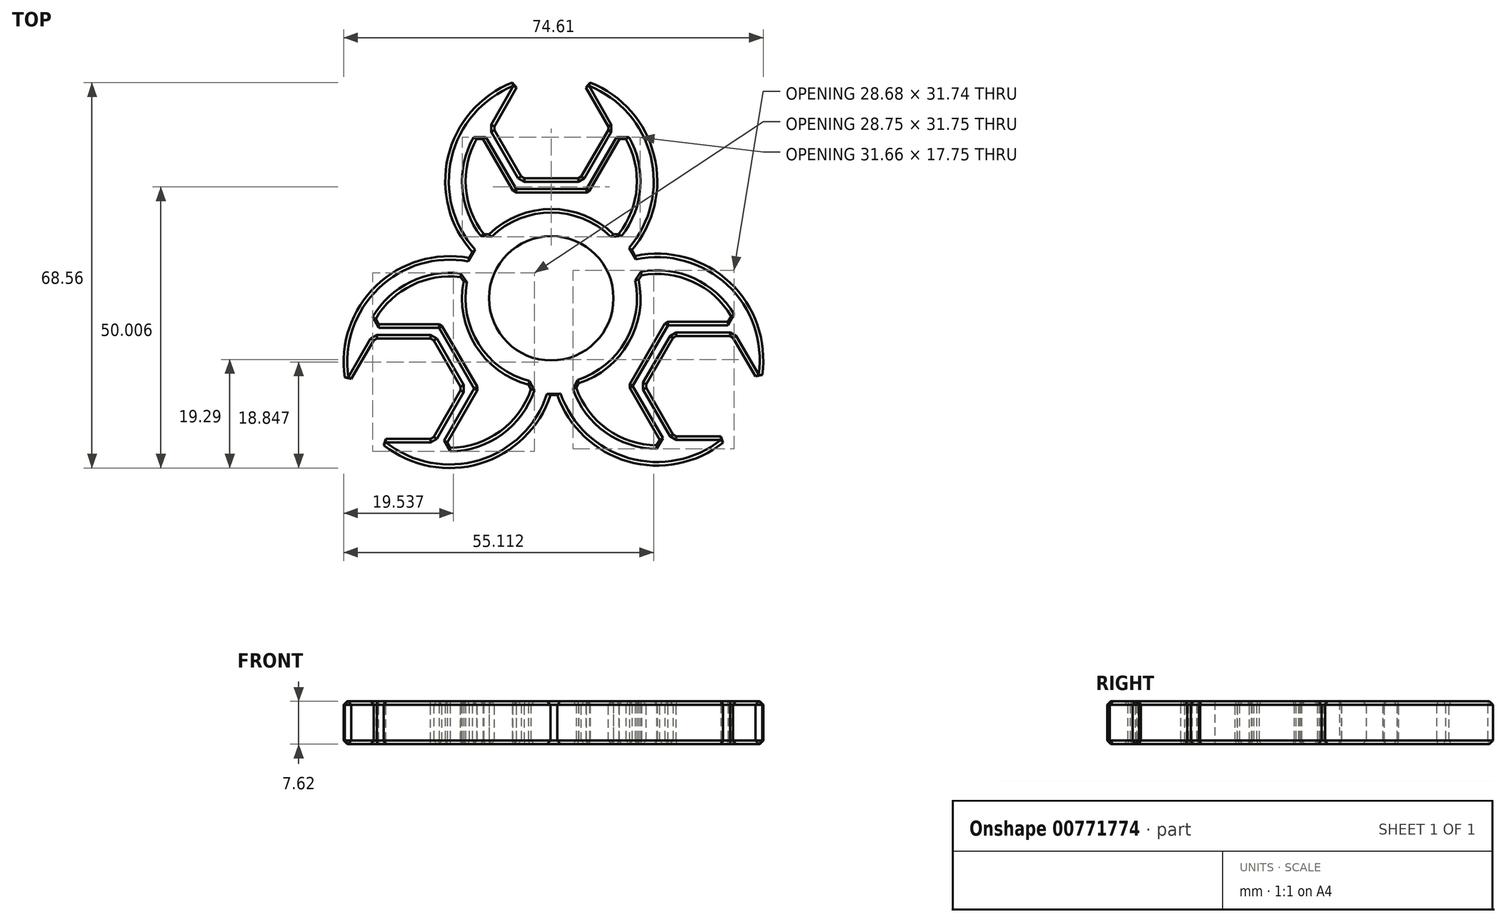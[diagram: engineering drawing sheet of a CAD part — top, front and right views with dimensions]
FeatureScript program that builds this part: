
annotation { "Feature Type Name" : "Feature", "Feature Type Description" : "" }
export const myFeature = defineFeature(function(context is Context, id is Id, definition is map)
    precondition{}
    {
        {
            var Q0;
            Q0=qCreatedBy(makeId("Top.planeOp"),FACE);
            var sketch = newSketch(context, id + "F0", { "sketchPlane" : qUnion([Q0])});
            skCircle(sketch, "E0", {"center": v(0, 0) * mm, "radius": 11.06 * mm});
            skCircle(sketch, "E1", {"center": v(0, 0) * mm, "radius": 15.88 * mm});
            skLineSegment(sketch, "E2", {"start": v(0, 0) * mm, "end": v(0, 15.88) * mm, "construction": true});
            skLineSegment(sketch, "E3", {"start": v(13.75, 7.94) * mm, "end": v(-13.75, 7.94) * mm, "construction": true});
            skPoint(sketch, "E3.startSnap0", {"position": v(0, 7.94) * mm});
            skLineSegment(sketch, "E4", {"start": v(0, 7.94) * mm, "end": v(0, 0) * mm, "construction": true});
            skLineSegment(sketch, "E5", {"start": v(0, 3.97) * mm, "end": v(0, 0) * mm, "construction": true});
            skCircle(sketch, "E6", {"center": v(0, 20.84) * mm, "radius": 18.85 * mm});
            skPoint(sketch, "E6.first.point", {"position": v(0, 1.98) * mm});
            skCircle(sketch, "E7", {"center": v(0, 20.84) * mm, "radius": 15.24 * mm});
            skLineSegment(sketch, "E8", {"start": v(0, 20.84) * mm, "end": v(0, 39.69) * mm, "construction": true});
            skPoint(sketch, "E9.0.midPoint", {"position": v(0, 45.97) * mm});
            skLineSegment(sketch, "E10", {"start": v(0, 20.84) * mm, "end": v(0, 30.26) * mm, "construction": true});
            skCircle(sketch, "E11.cCircle", {"center": v(0, 30.26) * mm, "radius": 8.93 * mm, "construction": true});
            skLineSegment(sketch, "E11.0", {"start": v(-5.16, 39.2) * mm, "end": v(5.16, 39.2) * mm});
            skLineSegment(sketch, "E11.1", {"start": v(5.16, 39.2) * mm, "end": v(10.31, 30.26) * mm});
            skLineSegment(sketch, "E11.2", {"start": v(10.31, 30.26) * mm, "end": v(5.16, 21.33) * mm});
            skLineSegment(sketch, "E11.3", {"start": v(5.16, 21.33) * mm, "end": v(-5.16, 21.33) * mm});
            skLineSegment(sketch, "E11.4", {"start": v(-5.16, 21.33) * mm, "end": v(-10.31, 30.26) * mm});
            skLineSegment(sketch, "E11.5", {"start": v(-10.31, 30.26) * mm, "end": v(-5.16, 39.2) * mm});
            skPoint(sketch, "E11.0.midPoint", {"position": v(0, 39.2) * mm});
            skLineSegment(sketch, "E12.1.0", {"start": v(-31.39, -7.13) * mm, "end": v(-21.08, -7.13) * mm});
            skPoint(sketch, "E12.1.1", {"position": v(-1.74, -1.93) * mm});
            skPoint(sketch, "E12.1.2", {"position": v(-6.9, -4.9) * mm});
            skLineSegment(sketch, "E12.1.3", {"start": v(-15.92, -16.06) * mm, "end": v(-21.08, -25) * mm});
            skPoint(sketch, "E12.1.4", {"position": v(-33.97, -20.53) * mm});
            skLineSegment(sketch, "E12.1.5", {"start": v(-21.08, -7.13) * mm, "end": v(-15.92, -16.06) * mm});
            skLineSegment(sketch, "E12.1.6", {"start": v(-18.07, -11.35) * mm, "end": v(-34.4, -20.78) * mm, "construction": true});
            skCircle(sketch, "E12.1.7", {"center": v(-18.07, -11.35) * mm, "radius": 18.85 * mm});
            skLineSegment(sketch, "E12.1.8", {"start": v(-18.07, -11.35) * mm, "end": v(-26.23, -16.06) * mm, "construction": true});
            skLineSegment(sketch, "E12.1.9", {"start": v(-31.39, -25) * mm, "end": v(-36.54, -16.06) * mm});
            skCircle(sketch, "E12.1.10", {"center": v(-26.23, -16.06) * mm, "radius": 8.93 * mm, "construction": true});
            skLineSegment(sketch, "E12.1.11", {"start": v(-36.54, -16.06) * mm, "end": v(-31.39, -7.13) * mm});
            skLineSegment(sketch, "E12.1.12", {"start": v(-13.77, 7) * mm, "end": v(-0.02, -16.8) * mm, "construction": true});
            skLineSegment(sketch, "E12.1.13", {"start": v(-21.08, -25) * mm, "end": v(-31.39, -25) * mm});
            skCircle(sketch, "E12.1.14", {"center": v(-18.07, -11.35) * mm, "radius": 15.24 * mm});
            skLineSegment(sketch, "E12.2.0", {"start": v(21.85, -24.55) * mm, "end": v(16.7, -15.62) * mm});
            skPoint(sketch, "E12.2.1", {"position": v(2.52, -1.48) * mm});
            skPoint(sketch, "E12.2.2", {"position": v(7.67, -4.46) * mm});
            skLineSegment(sketch, "E12.2.3", {"start": v(21.85, -6.69) * mm, "end": v(32.16, -6.69) * mm});
            skPoint(sketch, "E12.2.4", {"position": v(34.74, -20.08) * mm});
            skLineSegment(sketch, "E12.2.5", {"start": v(16.7, -15.62) * mm, "end": v(21.85, -6.69) * mm});
            skLineSegment(sketch, "E12.2.6", {"start": v(18.84, -10.9) * mm, "end": v(35.17, -20.33) * mm, "construction": true});
            skCircle(sketch, "E12.2.7", {"center": v(18.84, -10.9) * mm, "radius": 18.85 * mm});
            skLineSegment(sketch, "E12.2.8", {"start": v(18.84, -10.9) * mm, "end": v(27, -15.62) * mm, "construction": true});
            skLineSegment(sketch, "E12.2.9", {"start": v(37.32, -15.62) * mm, "end": v(32.16, -24.55) * mm});
            skCircle(sketch, "E12.2.10", {"center": v(27, -15.62) * mm, "radius": 8.93 * mm, "construction": true});
            skLineSegment(sketch, "E12.2.11", {"start": v(32.16, -24.55) * mm, "end": v(21.85, -24.55) * mm});
            skLineSegment(sketch, "E12.2.12", {"start": v(0.8, -16.36) * mm, "end": v(14.54, 7.45) * mm, "construction": true});
            skLineSegment(sketch, "E12.2.13", {"start": v(32.16, -6.69) * mm, "end": v(37.32, -15.62) * mm});
            skCircle(sketch, "E12.2.14", {"center": v(18.84, -10.9) * mm, "radius": 15.24 * mm});
            skPoint(sketch, "E12.center", {"position": v(0.26, -0.47) * mm});
            skCircle(sketch, "E13.cCircle", {"center": v(0, 30.26) * mm, "radius": 11.47 * mm, "construction": true});
            skLineSegment(sketch, "E13.0", {"start": v(-6.62, 41.73) * mm, "end": v(6.62, 41.73) * mm});
            skLineSegment(sketch, "E13.1", {"start": v(6.62, 41.73) * mm, "end": v(13.25, 30.26) * mm});
            skLineSegment(sketch, "E13.2", {"start": v(13.25, 30.26) * mm, "end": v(6.62, 18.8) * mm});
            skLineSegment(sketch, "E13.3", {"start": v(6.62, 18.8) * mm, "end": v(-6.62, 18.8) * mm});
            skLineSegment(sketch, "E13.4", {"start": v(-6.62, 18.8) * mm, "end": v(-13.25, 30.26) * mm});
            skLineSegment(sketch, "E13.5", {"start": v(-13.25, 30.26) * mm, "end": v(-6.62, 41.73) * mm});
            skPoint(sketch, "E13.0.midPoint", {"position": v(0, 41.73) * mm});
            skCircle(sketch, "E14.cCircle", {"center": v(27, -15.62) * mm, "radius": 11.47 * mm, "construction": true});
            skLineSegment(sketch, "E14.0", {"start": v(40.25, -15.62) * mm, "end": v(33.63, -27.09) * mm});
            skLineSegment(sketch, "E14.1", {"start": v(33.63, -27.09) * mm, "end": v(20.38, -27.09) * mm});
            skLineSegment(sketch, "E14.2", {"start": v(20.38, -27.09) * mm, "end": v(13.76, -15.62) * mm});
            skLineSegment(sketch, "E14.3", {"start": v(13.76, -15.62) * mm, "end": v(20.38, -4.15) * mm});
            skLineSegment(sketch, "E14.4", {"start": v(20.38, -4.15) * mm, "end": v(33.63, -4.15) * mm});
            skLineSegment(sketch, "E14.5", {"start": v(33.63, -4.15) * mm, "end": v(40.25, -15.62) * mm});
            skPoint(sketch, "E14.0.midPoint", {"position": v(36.94, -21.35) * mm});
            skCircle(sketch, "E15.cCircle", {"center": v(-26.23, -16.06) * mm, "radius": 11.47 * mm, "construction": true});
            skLineSegment(sketch, "E15.0", {"start": v(-32.85, -27.54) * mm, "end": v(-39.48, -16.06) * mm});
            skLineSegment(sketch, "E15.1", {"start": v(-39.48, -16.06) * mm, "end": v(-32.85, -4.6) * mm});
            skLineSegment(sketch, "E15.2", {"start": v(-32.85, -4.6) * mm, "end": v(-19.6, -4.6) * mm});
            skLineSegment(sketch, "E15.3", {"start": v(-19.6, -4.6) * mm, "end": v(-12.99, -16.06) * mm});
            skLineSegment(sketch, "E15.4", {"start": v(-12.99, -16.06) * mm, "end": v(-19.6, -27.54) * mm});
            skLineSegment(sketch, "E15.5", {"start": v(-19.6, -27.54) * mm, "end": v(-32.85, -27.54) * mm});
            skPoint(sketch, "E15.0.midPoint", {"position": v(-36.17, -21.8) * mm});
            skSolve(sketch);
        }
        {
            var Q0;
            {var subQ1=sQuery(id+"F0.wireOp",EDGE,"E6");var subQ7=sQuery(id+"F0.wireOp",EDGE,"E13.5");var subQ9=makeQuery(id+"F0.imprint","INTERSECT",VERTEX,{"derivedFrom":[subQ1,subQ7]});Q0=makeQuery(id+"F0.imprint","IMPRINT",FACE,{"disambiguationData":[TD([[makeQuery(id+"F0.imprint","IMPRINT",EDGE,{"disambiguationData":[TD([[subQ9,1.0]])],"derivedFrom":subQ1}),1.0]])]});}
            var Q1;
            {var subQ1=sQuery(id+"F0.wireOp",EDGE,"E1");var subQ5=sQuery(id+"F0.wireOp",EDGE,"E6");var subQ6=makeQuery(id+"F0.imprint","INTERSECT",VERTEX,{"disambiguationData":[OD(1.0)],"derivedFrom":[subQ1,subQ5]});Q1=makeQuery(id+"F0.imprint","IMPRINT",FACE,{"disambiguationData":[TD([[makeQuery(id+"F0.imprint","IMPRINT",EDGE,{"disambiguationData":[TD([[subQ6,1.0]])],"derivedFrom":subQ1}),-1.0]])]});}
            var Q2;
            {var subQ0=sQuery(id+"F0.wireOp",EDGE,"E11.2");Q2=makeQuery(id+"F0.imprint","IMPRINT",FACE,{"disambiguationData":[TD([[makeQuery(id+"F0.imprint","IMPRINT",EDGE,{"derivedFrom":subQ0}),1.0]])]});}
            var Q3;
            {var subQ1=sQuery(id+"F0.wireOp",EDGE,"E13.1");var subQ3=sQuery(id+"F0.wireOp",EDGE,"E6");var subQ4=makeQuery(id+"F0.imprint","INTERSECT",VERTEX,{"derivedFrom":[subQ3,subQ1]});Q3=makeQuery(id+"F0.imprint","IMPRINT",FACE,{"disambiguationData":[TD([[makeQuery(id+"F0.imprint","IMPRINT",EDGE,{"disambiguationData":[TD([[subQ4,-1.0]])],"derivedFrom":subQ3}),1.0]])]});}
            var Q4;
            {var subQ3=sQuery(id+"F0.wireOp",EDGE,"E6");var subQ6=sQuery(id+"F0.wireOp",EDGE,"E1");var subQ9=makeQuery(id+"F0.imprint","INTERSECT",VERTEX,{"disambiguationData":[OD(0.0)],"derivedFrom":[subQ6,subQ3]});Q4=makeQuery(id+"F0.imprint","IMPRINT",FACE,{"disambiguationData":[TD([[makeQuery(id+"F0.imprint","IMPRINT",EDGE,{"disambiguationData":[TD([[subQ9,-1.0]])],"derivedFrom":subQ6}),-1.0]])]});}
            var Q5;
            {var subQ0=sQuery(id+"F0.wireOp",EDGE,"E7");var subQ1=sQuery(id+"F0.wireOp",EDGE,"E0");var subQ2=makeQuery(id+"F0.imprint","INTERSECT",VERTEX,{"disambiguationData":[OD(0.0)],"derivedFrom":[subQ1,subQ0]});Q5=makeQuery(id+"F0.imprint","IMPRINT",FACE,{"disambiguationData":[TD([[makeQuery(id+"F0.imprint","IMPRINT",EDGE,{"disambiguationData":[TD([[subQ2,-1.0]])],"derivedFrom":subQ1}),-1.0]])]});}
            var Q6;
            {var subQ3=sQuery(id+"F0.wireOp",EDGE,"E12.2.7");var subQ7=sQuery(id+"F0.wireOp",EDGE,"E0");var subQ9=makeQuery(id+"F0.imprint","INTERSECT",VERTEX,{"disambiguationData":[OD(0.0)],"derivedFrom":[subQ7,subQ3]});Q6=makeQuery(id+"F0.imprint","IMPRINT",FACE,{"disambiguationData":[TD([[makeQuery(id+"F0.imprint","IMPRINT",EDGE,{"disambiguationData":[TD([[subQ9,-1.0]])],"derivedFrom":subQ7}),-1.0]])]});}
            var Q7;
            {var subQ3=sQuery(id+"F0.wireOp",EDGE,"E6");var subQ5=sQuery(id+"F0.wireOp",EDGE,"E0");var subQ6=makeQuery(id+"F0.imprint","INTERSECT",VERTEX,{"disambiguationData":[OD(1.0)],"derivedFrom":[subQ5,subQ3]});Q7=makeQuery(id+"F0.imprint","IMPRINT",FACE,{"disambiguationData":[TD([[makeQuery(id+"F0.imprint","IMPRINT",EDGE,{"disambiguationData":[TD([[subQ6,-1.0]])],"derivedFrom":subQ5}),-1.0]])]});}
            var Q8;
            {var subQ0=sQuery(id+"F0.wireOp",EDGE,"E12.1.7");var subQ1=sQuery(id+"F0.wireOp",EDGE,"E0");var subQ2=makeQuery(id+"F0.imprint","INTERSECT",VERTEX,{"disambiguationData":[OD(0.0)],"derivedFrom":[subQ1,subQ0]});Q8=makeQuery(id+"F0.imprint","IMPRINT",FACE,{"disambiguationData":[TD([[makeQuery(id+"F0.imprint","IMPRINT",EDGE,{"disambiguationData":[TD([[subQ2,-1.0]])],"derivedFrom":subQ1}),-1.0]])]});}
            var Q9;
            {var subQ0=sQuery(id+"F0.wireOp",EDGE,"E7");var subQ1=sQuery(id+"F0.wireOp",EDGE,"E0");var subQ2=makeQuery(id+"F0.imprint","INTERSECT",VERTEX,{"disambiguationData":[OD(1.0)],"derivedFrom":[subQ1,subQ0]});Q9=makeQuery(id+"F0.imprint","IMPRINT",FACE,{"disambiguationData":[TD([[makeQuery(id+"F0.imprint","IMPRINT",EDGE,{"disambiguationData":[TD([[subQ2,-1.0]])],"derivedFrom":subQ1}),-1.0]])]});}
            var Q10;
            {var subQ3=sQuery(id+"F0.wireOp",EDGE,"E6");var subQ5=sQuery(id+"F0.wireOp",EDGE,"E0");var subQ6=makeQuery(id+"F0.imprint","INTERSECT",VERTEX,{"disambiguationData":[OD(0.0)],"derivedFrom":[subQ5,subQ3]});Q10=makeQuery(id+"F0.imprint","IMPRINT",FACE,{"disambiguationData":[TD([[makeQuery(id+"F0.imprint","IMPRINT",EDGE,{"disambiguationData":[TD([[subQ6,1.0]])],"derivedFrom":subQ5}),-1.0]])]});}
            var Q11;
            {var subQ0=sQuery(id+"F0.wireOp",EDGE,"E6");var subQ1=sQuery(id+"F0.wireOp",EDGE,"E0");var subQ2=makeQuery(id+"F0.imprint","INTERSECT",VERTEX,{"disambiguationData":[OD(0.0)],"derivedFrom":[subQ1,subQ0]});Q11=makeQuery(id+"F0.imprint","IMPRINT",FACE,{"disambiguationData":[TD([[makeQuery(id+"F0.imprint","IMPRINT",EDGE,{"disambiguationData":[TD([[subQ2,-1.0]])],"derivedFrom":subQ1}),-1.0]])]});}
            var Q12;
            {var subQ5=sQuery(id+"F0.wireOp",EDGE,"E1");var subQ7=sQuery(id+"F0.wireOp",EDGE,"E12.2.7");var subQ8=makeQuery(id+"F0.imprint","INTERSECT",VERTEX,{"disambiguationData":[OD(0.0)],"derivedFrom":[subQ5,subQ7]});Q12=makeQuery(id+"F0.imprint","IMPRINT",FACE,{"disambiguationData":[TD([[makeQuery(id+"F0.imprint","IMPRINT",EDGE,{"disambiguationData":[TD([[subQ8,1.0]])],"derivedFrom":subQ5}),-1.0]])]});}
            var Q13;
            {var subQ0=sQuery(id+"F0.wireOp",EDGE,"E12.2.14");var subQ1=sQuery(id+"F0.wireOp",EDGE,"E0");var subQ2=makeQuery(id+"F0.imprint","INTERSECT",VERTEX,{"disambiguationData":[OD(0.0)],"derivedFrom":[subQ1,subQ0]});Q13=makeQuery(id+"F0.imprint","IMPRINT",FACE,{"disambiguationData":[TD([[makeQuery(id+"F0.imprint","IMPRINT",EDGE,{"disambiguationData":[TD([[subQ2,1.0]])],"derivedFrom":subQ1}),-1.0]])]});}
            var Q14;
            {var subQ0=sQuery(id+"F0.wireOp",EDGE,"E12.1.14");var subQ1=sQuery(id+"F0.wireOp",EDGE,"E0");var subQ2=makeQuery(id+"F0.imprint","INTERSECT",VERTEX,{"disambiguationData":[OD(0.0)],"derivedFrom":[subQ1,subQ0]});Q14=makeQuery(id+"F0.imprint","IMPRINT",FACE,{"disambiguationData":[TD([[makeQuery(id+"F0.imprint","IMPRINT",EDGE,{"disambiguationData":[TD([[subQ2,-1.0]])],"derivedFrom":subQ1}),-1.0]])]});}
            var Q15;
            {var subQ3=sQuery(id+"F0.wireOp",EDGE,"E12.1.7");var subQ5=sQuery(id+"F0.wireOp",EDGE,"E0");var subQ6=makeQuery(id+"F0.imprint","INTERSECT",VERTEX,{"disambiguationData":[OD(1.0)],"derivedFrom":[subQ5,subQ3]});Q15=makeQuery(id+"F0.imprint","IMPRINT",FACE,{"disambiguationData":[TD([[makeQuery(id+"F0.imprint","IMPRINT",EDGE,{"disambiguationData":[TD([[subQ6,-1.0]])],"derivedFrom":subQ5}),-1.0]])]});}
            var Q16;
            {var subQ0=sQuery(id+"F0.wireOp",EDGE,"E12.2.7");var subQ1=sQuery(id+"F0.wireOp",EDGE,"E0");var subQ2=makeQuery(id+"F0.imprint","INTERSECT",VERTEX,{"disambiguationData":[OD(1.0)],"derivedFrom":[subQ1,subQ0]});Q16=makeQuery(id+"F0.imprint","IMPRINT",FACE,{"disambiguationData":[TD([[makeQuery(id+"F0.imprint","IMPRINT",EDGE,{"disambiguationData":[TD([[subQ2,-1.0]])],"derivedFrom":subQ1}),-1.0]])]});}
            var Q17;
            {var subQ5=sQuery(id+"F0.wireOp",EDGE,"E12.1.14");var subQ6=sQuery(id+"F0.wireOp",EDGE,"E0");var subQ7=makeQuery(id+"F0.imprint","INTERSECT",VERTEX,{"disambiguationData":[OD(1.0)],"derivedFrom":[subQ6,subQ5]});Q17=makeQuery(id+"F0.imprint","IMPRINT",FACE,{"disambiguationData":[TD([[makeQuery(id+"F0.imprint","IMPRINT",EDGE,{"disambiguationData":[TD([[subQ7,-1.0]])],"derivedFrom":subQ6}),-1.0]])]});}
            var Q18;
            {var subQ5=sQuery(id+"F0.wireOp",EDGE,"E12.1.7");var subQ6=sQuery(id+"F0.wireOp",EDGE,"E1");var subQ7=makeQuery(id+"F0.imprint","INTERSECT",VERTEX,{"disambiguationData":[OD(1.0)],"derivedFrom":[subQ6,subQ5]});Q18=makeQuery(id+"F0.imprint","IMPRINT",FACE,{"disambiguationData":[TD([[makeQuery(id+"F0.imprint","IMPRINT",EDGE,{"disambiguationData":[TD([[subQ7,1.0]])],"derivedFrom":subQ6}),-1.0]])]});}
            var Q19;
            {var subQ3=sQuery(id+"F0.wireOp",EDGE,"E12.2.7");var subQ6=sQuery(id+"F0.wireOp",EDGE,"E1");var subQ9=makeQuery(id+"F0.imprint","INTERSECT",VERTEX,{"disambiguationData":[OD(1.0)],"derivedFrom":[subQ6,subQ3]});Q19=makeQuery(id+"F0.imprint","IMPRINT",FACE,{"disambiguationData":[TD([[makeQuery(id+"F0.imprint","IMPRINT",EDGE,{"disambiguationData":[TD([[subQ9,-1.0]])],"derivedFrom":subQ6}),-1.0]])]});}
            var Q20;
            {var subQ0=sQuery(id+"F0.wireOp",EDGE,"E14.5");var subQ7=sQuery(id+"F0.wireOp",EDGE,"E12.2.7");var subQ9=makeQuery(id+"F0.imprint","INTERSECT",VERTEX,{"derivedFrom":[subQ7,subQ0]});Q20=makeQuery(id+"F0.imprint","IMPRINT",FACE,{"disambiguationData":[TD([[makeQuery(id+"F0.imprint","IMPRINT",EDGE,{"disambiguationData":[TD([[subQ9,1.0]])],"derivedFrom":subQ7}),1.0]])]});}
            var Q21;
            {var subQ1=sQuery(id+"F0.wireOp",EDGE,"E12.2.0");Q21=makeQuery(id+"F0.imprint","IMPRINT",FACE,{"disambiguationData":[TD([[makeQuery(id+"F0.imprint","IMPRINT",EDGE,{"derivedFrom":subQ1}),1.0]])]});}
            var Q22;
            {var subQ1=sQuery(id+"F0.wireOp",EDGE,"E14.1");var subQ3=sQuery(id+"F0.wireOp",EDGE,"E12.2.7");var subQ4=makeQuery(id+"F0.imprint","INTERSECT",VERTEX,{"derivedFrom":[subQ3,subQ1]});Q22=makeQuery(id+"F0.imprint","IMPRINT",FACE,{"disambiguationData":[TD([[makeQuery(id+"F0.imprint","IMPRINT",EDGE,{"disambiguationData":[TD([[subQ4,-1.0]])],"derivedFrom":subQ3}),1.0]])]});}
            var Q23;
            {var subQ0=sQuery(id+"F0.wireOp",EDGE,"E15.5");var subQ7=sQuery(id+"F0.wireOp",EDGE,"E12.1.7");var subQ9=makeQuery(id+"F0.imprint","INTERSECT",VERTEX,{"derivedFrom":[subQ7,subQ0]});Q23=makeQuery(id+"F0.imprint","IMPRINT",FACE,{"disambiguationData":[TD([[makeQuery(id+"F0.imprint","IMPRINT",EDGE,{"disambiguationData":[TD([[subQ9,1.0]])],"derivedFrom":subQ7}),1.0]])]});}
            var Q24;
            {var subQ1=sQuery(id+"F0.wireOp",EDGE,"E12.1.0");Q24=makeQuery(id+"F0.imprint","IMPRINT",FACE,{"disambiguationData":[TD([[makeQuery(id+"F0.imprint","IMPRINT",EDGE,{"derivedFrom":subQ1}),1.0]])]});}
            var Q25;
            {var subQ1=sQuery(id+"F0.wireOp",EDGE,"E15.1");var subQ3=sQuery(id+"F0.wireOp",EDGE,"E12.1.7");var subQ4=makeQuery(id+"F0.imprint","INTERSECT",VERTEX,{"derivedFrom":[subQ3,subQ1]});Q25=makeQuery(id+"F0.imprint","IMPRINT",FACE,{"disambiguationData":[TD([[makeQuery(id+"F0.imprint","IMPRINT",EDGE,{"disambiguationData":[TD([[subQ4,-1.0]])],"derivedFrom":subQ3}),1.0]])]});}
            var Q26;
            {var subQ3=sQuery(id+"F0.wireOp",EDGE,"E12.1.7");var subQ6=sQuery(id+"F0.wireOp",EDGE,"E1");var subQ9=makeQuery(id+"F0.imprint","INTERSECT",VERTEX,{"disambiguationData":[OD(0.0)],"derivedFrom":[subQ6,subQ3]});Q26=makeQuery(id+"F0.imprint","IMPRINT",FACE,{"disambiguationData":[TD([[makeQuery(id+"F0.imprint","IMPRINT",EDGE,{"disambiguationData":[TD([[subQ9,-1.0]])],"derivedFrom":subQ6}),-1.0]])]});}
            extrude(context, id + "F1", {"entities" : qUnion([Q0, Q1, Q2, Q3, Q4, Q5, Q6, Q7, Q8, Q9, Q10, Q11, Q12, Q13, Q14, Q15, Q16, Q17, Q18, Q19, Q20, Q21, Q22, Q23, Q24, Q25, Q26]), "depth" : 7.62 * mm, "offsetDistance" : 25.4 * mm, "symmetric" : true});
        }
        {
            var Q0;
            {var subQ0=sQuery(id+"F0.wireOp",EDGE,"E6");var subQ1=makeQuery(id+"F0.imprint","INTERSECT",VERTEX,{"disambiguationData":[OD(1.0)],"derivedFrom":[sQuery(id+"F0.wireOp",EDGE,"E1"),subQ0]});var subQ2=makeQuery(id+"F0.imprint","INTERSECT",VERTEX,{"derivedFrom":[subQ0,sQuery(id+"F0.wireOp",EDGE,"E13.5")]});Q0=makeQuery(id+"F1.opExtrude","CAP_EDGE",EDGE,{"disambiguationData":[OSD([subQ0]),TDD([makeQuery(id+"F0.imprint","IMPRINT",EDGE,{"disambiguationData":[TD([[subQ2,1.0]])],"derivedFrom":subQ0}),makeQuery(id+"F0.imprint","IMPRINT",EDGE,{"disambiguationData":[TD([[subQ1,1.0]])],"derivedFrom":subQ0}),makeQuery(id+"F0.imprint","IMPRINT",EDGE,{"disambiguationData":[TD([[subQ1,-1.0]])],"derivedFrom":subQ0})])],"isStart":false});}
            var Q1;
            {var subQ0=sQuery(id+"F0.wireOp",EDGE,"E7");var subQ1=sQuery(id+"F0.wireOp",EDGE,"E1");Q1=makeQuery(id+"F1.opExtrude","CAP_EDGE",EDGE,{"disambiguationData":[OSD([subQ1]),TDD([makeQuery(id+"F0.imprint","IMPRINT",EDGE,{"disambiguationData":[TD([[makeQuery(id+"F0.imprint","INTERSECT",VERTEX,{"disambiguationData":[OD(0.0)],"derivedFrom":[subQ1,subQ0]}),-1.0]])],"derivedFrom":subQ1})])],"isStart":false});}
            var Q2;
            {var subQ0=sQuery(id+"F0.wireOp",EDGE,"E7");Q2=makeQuery(id+"F1.opExtrude","CAP_EDGE",EDGE,{"disambiguationData":[OSD([subQ0]),TDD([makeQuery(id+"F0.imprint","IMPRINT",EDGE,{"disambiguationData":[TD([[makeQuery(id+"F0.imprint","INTERSECT",VERTEX,{"disambiguationData":[OD(1.0)],"derivedFrom":[sQuery(id+"F0.wireOp",EDGE,"E1"),subQ0]}),1.0]])],"derivedFrom":subQ0})])],"isStart":false});}
            var Q3;
            Q3=makeQuery(id+"F1.opExtrude","CAP_EDGE",EDGE,{"disambiguationData":[OSD([sQuery(id+"F0.wireOp",EDGE,"E13.4")])],"isStart":false});
            var Q4;
            Q4=makeQuery(id+"F1.opExtrude","CAP_EDGE",EDGE,{"disambiguationData":[OSD([sQuery(id+"F0.wireOp",EDGE,"E13.3")])],"isStart":false});
            var Q5;
            Q5=makeQuery(id+"F1.opExtrude","CAP_EDGE",EDGE,{"disambiguationData":[OSD([sQuery(id+"F0.wireOp",EDGE,"E11.3")])],"isStart":false});
            var Q6;
            Q6=makeQuery(id+"F1.opExtrude","CAP_EDGE",EDGE,{"disambiguationData":[OSD([sQuery(id+"F0.wireOp",EDGE,"E11.4")])],"isStart":false});
            var Q7;
            Q7=makeQuery(id+"F1.opExtrude","CAP_EDGE",EDGE,{"disambiguationData":[OSD([sQuery(id+"F0.wireOp",EDGE,"E11.5")])],"isStart":false});
            var Q8;
            Q8=makeQuery(id+"F1.opExtrude","CAP_EDGE",EDGE,{"disambiguationData":[OSD([sQuery(id+"F0.wireOp",EDGE,"E11.1")])],"isStart":false});
            var Q9;
            Q9=makeQuery(id+"F1.opExtrude","CAP_EDGE",EDGE,{"disambiguationData":[OSD([sQuery(id+"F0.wireOp",EDGE,"E11.2")])],"isStart":false});
            var Q10;
            {var subQ0=sQuery(id+"F0.wireOp",EDGE,"E6");var subQ1=makeQuery(id+"F0.imprint","INTERSECT",VERTEX,{"disambiguationData":[OD(0.0)],"derivedFrom":[sQuery(id+"F0.wireOp",EDGE,"E1"),subQ0]});var subQ2=makeQuery(id+"F0.imprint","INTERSECT",VERTEX,{"derivedFrom":[subQ0,sQuery(id+"F0.wireOp",EDGE,"E13.1")]});Q10=makeQuery(id+"F1.opExtrude","CAP_EDGE",EDGE,{"disambiguationData":[OSD([subQ0]),TDD([makeQuery(id+"F0.imprint","IMPRINT",EDGE,{"disambiguationData":[TD([[subQ2,-1.0]])],"derivedFrom":subQ0}),makeQuery(id+"F0.imprint","IMPRINT",EDGE,{"disambiguationData":[TD([[subQ1,1.0]])],"derivedFrom":subQ0}),makeQuery(id+"F0.imprint","IMPRINT",EDGE,{"disambiguationData":[TD([[subQ1,-1.0]])],"derivedFrom":subQ0})])],"isStart":false});}
            var Q11;
            Q11=makeQuery(id+"F1.opExtrude","CAP_EDGE",EDGE,{"disambiguationData":[OSD([sQuery(id+"F0.wireOp",EDGE,"E13.2")])],"isStart":false});
            var Q12;
            {var subQ0=sQuery(id+"F0.wireOp",EDGE,"E7");Q12=makeQuery(id+"F1.opExtrude","CAP_EDGE",EDGE,{"disambiguationData":[OSD([subQ0]),TDD([makeQuery(id+"F0.imprint","IMPRINT",EDGE,{"disambiguationData":[TD([[makeQuery(id+"F0.imprint","INTERSECT",VERTEX,{"disambiguationData":[OD(0.0)],"derivedFrom":[sQuery(id+"F0.wireOp",EDGE,"E1"),subQ0]}),-1.0]])],"derivedFrom":subQ0})])],"isStart":false});}
            var Q13;
            {var subQ0=sQuery(id+"F0.wireOp",EDGE,"E12.2.7");var subQ1=makeQuery(id+"F0.imprint","INTERSECT",VERTEX,{"disambiguationData":[OD(0.0)],"derivedFrom":[sQuery(id+"F0.wireOp",EDGE,"E1"),subQ0]});var subQ2=makeQuery(id+"F0.imprint","INTERSECT",VERTEX,{"derivedFrom":[subQ0,sQuery(id+"F0.wireOp",EDGE,"E14.5")]});Q13=makeQuery(id+"F1.opExtrude","CAP_EDGE",EDGE,{"disambiguationData":[OSD([subQ0]),TDD([makeQuery(id+"F0.imprint","IMPRINT",EDGE,{"disambiguationData":[TD([[subQ2,1.0]])],"derivedFrom":subQ0}),makeQuery(id+"F0.imprint","IMPRINT",EDGE,{"disambiguationData":[TD([[subQ1,1.0]])],"derivedFrom":subQ0}),makeQuery(id+"F0.imprint","IMPRINT",EDGE,{"disambiguationData":[TD([[subQ1,-1.0]])],"derivedFrom":subQ0})])],"isStart":false});}
            var Q14;
            {var subQ0=sQuery(id+"F0.wireOp",EDGE,"E12.2.14");Q14=makeQuery(id+"F1.opExtrude","CAP_EDGE",EDGE,{"disambiguationData":[OSD([subQ0]),TDD([makeQuery(id+"F0.imprint","IMPRINT",EDGE,{"disambiguationData":[TD([[makeQuery(id+"F0.imprint","INTERSECT",VERTEX,{"disambiguationData":[OD(0.0)],"derivedFrom":[sQuery(id+"F0.wireOp",EDGE,"E1"),subQ0]}),1.0]])],"derivedFrom":subQ0})])],"isStart":false});}
            var Q15;
            Q15=makeQuery(id+"F1.opExtrude","CAP_EDGE",EDGE,{"disambiguationData":[OSD([sQuery(id+"F0.wireOp",EDGE,"E12.2.3")])],"isStart":false});
            var Q16;
            Q16=makeQuery(id+"F1.opExtrude","CAP_EDGE",EDGE,{"disambiguationData":[OSD([sQuery(id+"F0.wireOp",EDGE,"E12.2.13")])],"isStart":false});
            var Q17;
            Q17=makeQuery(id+"F1.opExtrude","CAP_EDGE",EDGE,{"disambiguationData":[OSD([sQuery(id+"F0.wireOp",EDGE,"E12.2.5")])],"isStart":false});
            var Q18;
            Q18=makeQuery(id+"F1.opExtrude","CAP_EDGE",EDGE,{"disambiguationData":[OSD([sQuery(id+"F0.wireOp",EDGE,"E12.2.0")])],"isStart":false});
            var Q19;
            Q19=makeQuery(id+"F1.opExtrude","CAP_EDGE",EDGE,{"disambiguationData":[OSD([sQuery(id+"F0.wireOp",EDGE,"E12.2.11")])],"isStart":false});
            var Q20;
            {var subQ0=sQuery(id+"F0.wireOp",EDGE,"E12.2.7");var subQ1=makeQuery(id+"F0.imprint","INTERSECT",VERTEX,{"disambiguationData":[OD(1.0)],"derivedFrom":[sQuery(id+"F0.wireOp",EDGE,"E1"),subQ0]});var subQ2=makeQuery(id+"F0.imprint","INTERSECT",VERTEX,{"derivedFrom":[subQ0,sQuery(id+"F0.wireOp",EDGE,"E14.1")]});Q20=makeQuery(id+"F1.opExtrude","CAP_EDGE",EDGE,{"disambiguationData":[OSD([subQ0]),TDD([makeQuery(id+"F0.imprint","IMPRINT",EDGE,{"disambiguationData":[TD([[subQ2,-1.0]])],"derivedFrom":subQ0}),makeQuery(id+"F0.imprint","IMPRINT",EDGE,{"disambiguationData":[TD([[subQ1,1.0]])],"derivedFrom":subQ0}),makeQuery(id+"F0.imprint","IMPRINT",EDGE,{"disambiguationData":[TD([[subQ1,-1.0]])],"derivedFrom":subQ0})])],"isStart":false});}
            var Q21;
            Q21=makeQuery(id+"F1.opExtrude","CAP_EDGE",EDGE,{"disambiguationData":[OSD([sQuery(id+"F0.wireOp",EDGE,"E14.2")])],"isStart":false});
            var Q22;
            Q22=makeQuery(id+"F1.opExtrude","CAP_EDGE",EDGE,{"disambiguationData":[OSD([sQuery(id+"F0.wireOp",EDGE,"E14.3")])],"isStart":false});
            var Q23;
            Q23=makeQuery(id+"F1.opExtrude","CAP_EDGE",EDGE,{"disambiguationData":[OSD([sQuery(id+"F0.wireOp",EDGE,"E14.4")])],"isStart":false});
            var Q24;
            {var subQ0=sQuery(id+"F0.wireOp",EDGE,"E12.2.14");Q24=makeQuery(id+"F1.opExtrude","CAP_EDGE",EDGE,{"disambiguationData":[OSD([subQ0]),TDD([makeQuery(id+"F0.imprint","IMPRINT",EDGE,{"disambiguationData":[TD([[makeQuery(id+"F0.imprint","INTERSECT",VERTEX,{"disambiguationData":[OD(1.0)],"derivedFrom":[sQuery(id+"F0.wireOp",EDGE,"E1"),subQ0]}),-1.0]])],"derivedFrom":subQ0})])],"isStart":false});}
            var Q25;
            {var subQ0=sQuery(id+"F0.wireOp",EDGE,"E12.2.14");var subQ1=sQuery(id+"F0.wireOp",EDGE,"E1");Q25=makeQuery(id+"F1.opExtrude","CAP_EDGE",EDGE,{"disambiguationData":[OSD([subQ1]),TDD([makeQuery(id+"F0.imprint","IMPRINT",EDGE,{"disambiguationData":[TD([[makeQuery(id+"F0.imprint","INTERSECT",VERTEX,{"disambiguationData":[OD(0.0)],"derivedFrom":[subQ1,subQ0]}),1.0]])],"derivedFrom":subQ1})])],"isStart":false});}
            var Q26;
            {var subQ0=sQuery(id+"F0.wireOp",EDGE,"E12.1.7");var subQ1=makeQuery(id+"F0.imprint","INTERSECT",VERTEX,{"disambiguationData":[OD(1.0)],"derivedFrom":[sQuery(id+"F0.wireOp",EDGE,"E1"),subQ0]});var subQ2=makeQuery(id+"F0.imprint","INTERSECT",VERTEX,{"derivedFrom":[subQ0,sQuery(id+"F0.wireOp",EDGE,"E15.5")]});Q26=makeQuery(id+"F1.opExtrude","CAP_EDGE",EDGE,{"disambiguationData":[OSD([subQ0]),TDD([makeQuery(id+"F0.imprint","IMPRINT",EDGE,{"disambiguationData":[TD([[subQ2,1.0]])],"derivedFrom":subQ0}),makeQuery(id+"F0.imprint","IMPRINT",EDGE,{"disambiguationData":[TD([[subQ1,1.0]])],"derivedFrom":subQ0}),makeQuery(id+"F0.imprint","IMPRINT",EDGE,{"disambiguationData":[TD([[subQ1,-1.0]])],"derivedFrom":subQ0})])],"isStart":false});}
            var Q27;
            {var subQ0=sQuery(id+"F0.wireOp",EDGE,"E12.1.14");Q27=makeQuery(id+"F1.opExtrude","CAP_EDGE",EDGE,{"disambiguationData":[OSD([subQ0]),TDD([makeQuery(id+"F0.imprint","IMPRINT",EDGE,{"disambiguationData":[TD([[makeQuery(id+"F0.imprint","INTERSECT",VERTEX,{"disambiguationData":[OD(1.0)],"derivedFrom":[sQuery(id+"F0.wireOp",EDGE,"E1"),subQ0]}),1.0]])],"derivedFrom":subQ0})])],"isStart":false});}
            var Q28;
            Q28=makeQuery(id+"F1.opExtrude","CAP_EDGE",EDGE,{"disambiguationData":[OSD([sQuery(id+"F0.wireOp",EDGE,"E15.4")])],"isStart":false});
            var Q29;
            Q29=makeQuery(id+"F1.opExtrude","CAP_EDGE",EDGE,{"disambiguationData":[OSD([sQuery(id+"F0.wireOp",EDGE,"E12.1.3")])],"isStart":false});
            var Q30;
            Q30=makeQuery(id+"F1.opExtrude","CAP_EDGE",EDGE,{"disambiguationData":[OSD([sQuery(id+"F0.wireOp",EDGE,"E12.1.13")])],"isStart":false});
            var Q31;
            Q31=makeQuery(id+"F1.opExtrude","CAP_EDGE",EDGE,{"disambiguationData":[OSD([sQuery(id+"F0.wireOp",EDGE,"E12.1.5")])],"isStart":false});
            var Q32;
            Q32=makeQuery(id+"F1.opExtrude","CAP_EDGE",EDGE,{"disambiguationData":[OSD([sQuery(id+"F0.wireOp",EDGE,"E15.3")])],"isStart":false});
            var Q33;
            Q33=makeQuery(id+"F1.opExtrude","CAP_EDGE",EDGE,{"disambiguationData":[OSD([sQuery(id+"F0.wireOp",EDGE,"E15.2")])],"isStart":false});
            var Q34;
            Q34=makeQuery(id+"F1.opExtrude","CAP_EDGE",EDGE,{"disambiguationData":[OSD([sQuery(id+"F0.wireOp",EDGE,"E12.1.0")])],"isStart":false});
            var Q35;
            Q35=makeQuery(id+"F1.opExtrude","CAP_EDGE",EDGE,{"disambiguationData":[OSD([sQuery(id+"F0.wireOp",EDGE,"E12.1.11")])],"isStart":false});
            var Q36;
            {var subQ0=sQuery(id+"F0.wireOp",EDGE,"E12.1.7");var subQ1=makeQuery(id+"F0.imprint","INTERSECT",VERTEX,{"disambiguationData":[OD(0.0)],"derivedFrom":[sQuery(id+"F0.wireOp",EDGE,"E1"),subQ0]});var subQ2=makeQuery(id+"F0.imprint","INTERSECT",VERTEX,{"derivedFrom":[subQ0,sQuery(id+"F0.wireOp",EDGE,"E15.1")]});Q36=makeQuery(id+"F1.opExtrude","CAP_EDGE",EDGE,{"disambiguationData":[OSD([subQ0]),TDD([makeQuery(id+"F0.imprint","IMPRINT",EDGE,{"disambiguationData":[TD([[subQ2,-1.0]])],"derivedFrom":subQ0}),makeQuery(id+"F0.imprint","IMPRINT",EDGE,{"disambiguationData":[TD([[subQ1,1.0]])],"derivedFrom":subQ0}),makeQuery(id+"F0.imprint","IMPRINT",EDGE,{"disambiguationData":[TD([[subQ1,-1.0]])],"derivedFrom":subQ0})])],"isStart":false});}
            var Q37;
            {var subQ0=sQuery(id+"F0.wireOp",EDGE,"E12.1.14");var subQ1=sQuery(id+"F0.wireOp",EDGE,"E1");Q37=makeQuery(id+"F1.opExtrude","CAP_EDGE",EDGE,{"disambiguationData":[OSD([subQ1]),TDD([makeQuery(id+"F0.imprint","IMPRINT",EDGE,{"disambiguationData":[TD([[makeQuery(id+"F0.imprint","INTERSECT",VERTEX,{"disambiguationData":[OD(0.0)],"derivedFrom":[subQ1,subQ0]}),-1.0]])],"derivedFrom":subQ1})])],"isStart":false});}
            var Q38;
            {var subQ0=sQuery(id+"F0.wireOp",EDGE,"E12.1.14");Q38=makeQuery(id+"F1.opExtrude","CAP_EDGE",EDGE,{"disambiguationData":[OSD([subQ0]),TDD([makeQuery(id+"F0.imprint","IMPRINT",EDGE,{"disambiguationData":[TD([[makeQuery(id+"F0.imprint","INTERSECT",VERTEX,{"disambiguationData":[OD(0.0)],"derivedFrom":[sQuery(id+"F0.wireOp",EDGE,"E1"),subQ0]}),-1.0]])],"derivedFrom":subQ0})])],"isStart":false});}
            var Q39;
            Q39=makeQuery(id+"F1.opExtrude","CAP_EDGE",EDGE,{"disambiguationData":[OSD([sQuery(id+"F0.wireOp",EDGE,"E12.1.11")])],"isStart":true});
            var Q40;
            Q40=makeQuery(id+"F1.opExtrude","CAP_EDGE",EDGE,{"disambiguationData":[OSD([sQuery(id+"F0.wireOp",EDGE,"E12.1.0")])],"isStart":true});
            var Q41;
            Q41=makeQuery(id+"F1.opExtrude","CAP_EDGE",EDGE,{"disambiguationData":[OSD([sQuery(id+"F0.wireOp",EDGE,"E15.2")])],"isStart":true});
            var Q42;
            {var subQ0=sQuery(id+"F0.wireOp",EDGE,"E12.1.14");Q42=makeQuery(id+"F1.opExtrude","CAP_EDGE",EDGE,{"disambiguationData":[OSD([subQ0]),TDD([makeQuery(id+"F0.imprint","IMPRINT",EDGE,{"disambiguationData":[TD([[makeQuery(id+"F0.imprint","INTERSECT",VERTEX,{"disambiguationData":[OD(0.0)],"derivedFrom":[sQuery(id+"F0.wireOp",EDGE,"E1"),subQ0]}),-1.0]])],"derivedFrom":subQ0})])],"isStart":true});}
            var Q43;
            {var subQ0=sQuery(id+"F0.wireOp",EDGE,"E12.1.7");var subQ1=makeQuery(id+"F0.imprint","INTERSECT",VERTEX,{"disambiguationData":[OD(0.0)],"derivedFrom":[sQuery(id+"F0.wireOp",EDGE,"E1"),subQ0]});var subQ2=makeQuery(id+"F0.imprint","INTERSECT",VERTEX,{"derivedFrom":[subQ0,sQuery(id+"F0.wireOp",EDGE,"E15.1")]});Q43=makeQuery(id+"F1.opExtrude","CAP_EDGE",EDGE,{"disambiguationData":[OSD([subQ0]),TDD([makeQuery(id+"F0.imprint","IMPRINT",EDGE,{"disambiguationData":[TD([[subQ2,-1.0]])],"derivedFrom":subQ0}),makeQuery(id+"F0.imprint","IMPRINT",EDGE,{"disambiguationData":[TD([[subQ1,1.0]])],"derivedFrom":subQ0}),makeQuery(id+"F0.imprint","IMPRINT",EDGE,{"disambiguationData":[TD([[subQ1,-1.0]])],"derivedFrom":subQ0})])],"isStart":true});}
            var Q44;
            Q44=makeQuery(id+"F1.opExtrude","SWEPT_EDGE",EDGE,{"disambiguationData":[OSD([sQuery(id+"F0.wireOp",EDGE,"E11.3"),sQuery(id+"F0.wireOp",EDGE,"E11.4")])]});
            var Q45;
            Q45=makeQuery(id+"F1.opExtrude","SWEPT_EDGE",EDGE,{"disambiguationData":[OSD([sQuery(id+"F0.wireOp",EDGE,"E12.2.0"),sQuery(id+"F0.wireOp",EDGE,"E12.2.11")])]});
            var Q46;
            Q46=makeQuery(id+"F1.opExtrude","CAP_EDGE",EDGE,{"disambiguationData":[OSD([sQuery(id+"F0.wireOp",EDGE,"E12.1.13")])],"isStart":true});
            var Q47;
            Q47=makeQuery(id+"F1.opExtrude","CAP_EDGE",EDGE,{"disambiguationData":[OSD([sQuery(id+"F0.wireOp",EDGE,"E12.2.11")])],"isStart":true});
            var Q48;
            Q48=makeQuery(id+"F1.opExtrude","CAP_EDGE",EDGE,{"disambiguationData":[OSD([sQuery(id+"F0.wireOp",EDGE,"E12.2.3")])],"isStart":true});
            var Q49;
            Q49=makeQuery(id+"F1.opExtrude","CAP_EDGE",EDGE,{"disambiguationData":[OSD([sQuery(id+"F0.wireOp",EDGE,"E11.3")])],"isStart":true});
            var Q50;
            Q50=makeQuery(id+"F1.opExtrude","SWEPT_EDGE",EDGE,{"disambiguationData":[OSD([sQuery(id+"F0.wireOp",EDGE,"E13.3"),sQuery(id+"F0.wireOp",EDGE,"E13.4")])]});
            var Q51;
            Q51=makeQuery(id+"F1.opExtrude","SWEPT_EDGE",EDGE,{"disambiguationData":[OSD([sQuery(id+"F0.wireOp",EDGE,"E14.2"),sQuery(id+"F0.wireOp",EDGE,"E14.3")])]});
            var Q52;
            Q52=makeQuery(id+"F1.opExtrude","SWEPT_EDGE",EDGE,{"disambiguationData":[OSD([sQuery(id+"F0.wireOp",EDGE,"E14.3"),sQuery(id+"F0.wireOp",EDGE,"E14.4")])]});
            var Q53;
            Q53=makeQuery(id+"F1.opExtrude","SWEPT_EDGE",EDGE,{"disambiguationData":[OSD([sQuery(id+"F0.wireOp",EDGE,"E11.4"),sQuery(id+"F0.wireOp",EDGE,"E11.5")])]});
            var Q54;
            Q54=makeQuery(id+"F1.opExtrude","SWEPT_EDGE",EDGE,{"disambiguationData":[OSD([sQuery(id+"F0.wireOp",EDGE,"E12.1.3"),sQuery(id+"F0.wireOp",EDGE,"E12.1.13")])]});
            var Q55;
            Q55=makeQuery(id+"F1.opExtrude","SWEPT_EDGE",EDGE,{"disambiguationData":[OSD([sQuery(id+"F0.wireOp",EDGE,"E12.2.0"),sQuery(id+"F0.wireOp",EDGE,"E12.2.5")])]});
            var Q56;
            Q56=makeQuery(id+"F1.opExtrude","SWEPT_EDGE",EDGE,{"disambiguationData":[OSD([sQuery(id+"F0.wireOp",EDGE,"E12.2.3"),sQuery(id+"F0.wireOp",EDGE,"E12.2.5")])]});
            var Q57;
            Q57=makeQuery(id+"F1.opExtrude","SWEPT_EDGE",EDGE,{"disambiguationData":[OSD([sQuery(id+"F0.wireOp",EDGE,"E13.2"),sQuery(id+"F0.wireOp",EDGE,"E13.3")])]});
            var Q58;
            {var subQ0=sQuery(id+"F0.wireOp",EDGE,"E12.2.14");var subQ1=sQuery(id+"F0.wireOp",EDGE,"E1");Q58=makeQuery(id+"F1.opExtrude","CAP_EDGE",EDGE,{"disambiguationData":[OSD([subQ1]),TDD([makeQuery(id+"F0.imprint","IMPRINT",EDGE,{"disambiguationData":[TD([[makeQuery(id+"F0.imprint","INTERSECT",VERTEX,{"disambiguationData":[OD(0.0)],"derivedFrom":[subQ1,subQ0]}),1.0]])],"derivedFrom":subQ1})])],"isStart":true});}
            var Q59;
            Q59=makeQuery(id+"F1.opExtrude","CAP_EDGE",EDGE,{"disambiguationData":[OSD([sQuery(id+"F0.wireOp",EDGE,"E11.4")])],"isStart":true});
            var Q60;
            Q60=makeQuery(id+"F1.opExtrude","CAP_EDGE",EDGE,{"disambiguationData":[OSD([sQuery(id+"F0.wireOp",EDGE,"E14.3")])],"isStart":true});
            var Q61;
            Q61=makeQuery(id+"F1.opExtrude","SWEPT_EDGE",EDGE,{"disambiguationData":[OSD([sQuery(id+"F0.wireOp",EDGE,"E12.1.7"),sQuery(id+"F0.wireOp",EDGE,"E12.1.11")])]});
            var Q62;
            Q62=makeQuery(id+"F1.opExtrude","SWEPT_EDGE",EDGE,{"disambiguationData":[OSD([sQuery(id+"F0.wireOp",EDGE,"E12.1.7"),sQuery(id+"F0.wireOp",EDGE,"E12.1.13")])]});
            var Q63;
            {var subQ0=sQuery(id+"F0.wireOp",EDGE,"E6");var subQ1=makeQuery(id+"F0.imprint","INTERSECT",VERTEX,{"disambiguationData":[OD(0.0)],"derivedFrom":[sQuery(id+"F0.wireOp",EDGE,"E1"),subQ0]});var subQ2=makeQuery(id+"F0.imprint","INTERSECT",VERTEX,{"derivedFrom":[subQ0,sQuery(id+"F0.wireOp",EDGE,"E13.1")]});Q63=makeQuery(id+"F1.opExtrude","CAP_EDGE",EDGE,{"disambiguationData":[OSD([subQ0]),TDD([makeQuery(id+"F0.imprint","IMPRINT",EDGE,{"disambiguationData":[TD([[subQ2,-1.0]])],"derivedFrom":subQ0}),makeQuery(id+"F0.imprint","IMPRINT",EDGE,{"disambiguationData":[TD([[subQ1,1.0]])],"derivedFrom":subQ0}),makeQuery(id+"F0.imprint","IMPRINT",EDGE,{"disambiguationData":[TD([[subQ1,-1.0]])],"derivedFrom":subQ0})])],"isStart":true});}
            var Q64;
            Q64=makeQuery(id+"F1.opExtrude","CAP_EDGE",EDGE,{"disambiguationData":[OSD([sQuery(id+"F0.wireOp",EDGE,"E11.5")])],"isStart":true});
            var Q65;
            {var subQ0=sQuery(id+"F0.wireOp",EDGE,"E12.1.14");Q65=makeQuery(id+"F1.opExtrude","CAP_EDGE",EDGE,{"disambiguationData":[OSD([subQ0]),TDD([makeQuery(id+"F0.imprint","IMPRINT",EDGE,{"disambiguationData":[TD([[makeQuery(id+"F0.imprint","INTERSECT",VERTEX,{"disambiguationData":[OD(1.0)],"derivedFrom":[sQuery(id+"F0.wireOp",EDGE,"E1"),subQ0]}),1.0]])],"derivedFrom":subQ0})])],"isStart":true});}
            var Q66;
            Q66=makeQuery(id+"F1.opExtrude","CAP_EDGE",EDGE,{"disambiguationData":[OSD([sQuery(id+"F0.wireOp",EDGE,"E12.2.13")])],"isStart":true});
            var Q67;
            Q67=makeQuery(id+"F1.opExtrude","CAP_EDGE",EDGE,{"disambiguationData":[OSD([sQuery(id+"F0.wireOp",EDGE,"E14.4")])],"isStart":true});
            var Q68;
            Q68=makeQuery(id+"F1.opExtrude","SWEPT_EDGE",EDGE,{"disambiguationData":[OSD([sQuery(id+"F0.wireOp",EDGE,"E15.2"),sQuery(id+"F0.wireOp",EDGE,"E15.3")])]});
            var Q69;
            Q69=makeQuery(id+"F1.opExtrude","SWEPT_EDGE",EDGE,{"disambiguationData":[OSD([sQuery(id+"F0.wireOp",EDGE,"E12.1.7"),sQuery(id+"F0.wireOp",EDGE,"E12.2.7")])]});
            var Q70;
            Q70=makeQuery(id+"F1.opExtrude","SWEPT_EDGE",EDGE,{"disambiguationData":[OSD([sQuery(id+"F0.wireOp",EDGE,"E15.3"),sQuery(id+"F0.wireOp",EDGE,"E15.4")])]});
            var Q71;
            Q71=makeQuery(id+"F1.opExtrude","SWEPT_EDGE",EDGE,{"disambiguationData":[OSD([sQuery(id+"F0.wireOp",EDGE,"E12.1.14"),sQuery(id+"F0.wireOp",EDGE,"E15.2")])]});
            var Q72;
            {var subQ0=sQuery(id+"F0.wireOp",EDGE,"E6");var subQ1=makeQuery(id+"F0.imprint","INTERSECT",VERTEX,{"disambiguationData":[OD(1.0)],"derivedFrom":[sQuery(id+"F0.wireOp",EDGE,"E1"),subQ0]});var subQ2=makeQuery(id+"F0.imprint","INTERSECT",VERTEX,{"derivedFrom":[subQ0,sQuery(id+"F0.wireOp",EDGE,"E13.5")]});Q72=makeQuery(id+"F1.opExtrude","CAP_EDGE",EDGE,{"disambiguationData":[OSD([subQ0]),TDD([makeQuery(id+"F0.imprint","IMPRINT",EDGE,{"disambiguationData":[TD([[subQ2,1.0]])],"derivedFrom":subQ0}),makeQuery(id+"F0.imprint","IMPRINT",EDGE,{"disambiguationData":[TD([[subQ1,1.0]])],"derivedFrom":subQ0}),makeQuery(id+"F0.imprint","IMPRINT",EDGE,{"disambiguationData":[TD([[subQ1,-1.0]])],"derivedFrom":subQ0})])],"isStart":true});}
            var Q73;
            {var subQ0=sQuery(id+"F0.wireOp",EDGE,"E12.2.14");Q73=makeQuery(id+"F1.opExtrude","CAP_EDGE",EDGE,{"disambiguationData":[OSD([subQ0]),TDD([makeQuery(id+"F0.imprint","IMPRINT",EDGE,{"disambiguationData":[TD([[makeQuery(id+"F0.imprint","INTERSECT",VERTEX,{"disambiguationData":[OD(0.0)],"derivedFrom":[sQuery(id+"F0.wireOp",EDGE,"E1"),subQ0]}),1.0]])],"derivedFrom":subQ0})])],"isStart":true});}
            var Q74;
            Q74=makeQuery(id+"F1.opExtrude","SWEPT_EDGE",EDGE,{"disambiguationData":[OSD([sQuery(id+"F0.wireOp",EDGE,"E12.1.14"),sQuery(id+"F0.wireOp",EDGE,"E15.4")])]});
            var Q75;
            {var subQ0=sQuery(id+"F0.wireOp",EDGE,"E7");var subQ1=sQuery(id+"F0.wireOp",EDGE,"E1");Q75=makeQuery(id+"F1.opExtrude","SWEPT_EDGE",EDGE,{"disambiguationData":[OSD([subQ1,subQ0]),TDD([makeQuery(id+"F0.imprint","INTERSECT",VERTEX,{"disambiguationData":[OD(0.0)],"derivedFrom":[subQ1,subQ0]})])]});}
            var Q76;
            Q76=makeQuery(id+"F1.opExtrude","SWEPT_EDGE",EDGE,{"disambiguationData":[OSD([sQuery(id+"F0.wireOp",EDGE,"E12.2.7"),sQuery(id+"F0.wireOp",EDGE,"E12.2.11")])]});
            var Q77;
            {var subQ0=sQuery(id+"F0.wireOp",EDGE,"E7");Q77=makeQuery(id+"F1.opExtrude","CAP_EDGE",EDGE,{"disambiguationData":[OSD([subQ0]),TDD([makeQuery(id+"F0.imprint","IMPRINT",EDGE,{"disambiguationData":[TD([[makeQuery(id+"F0.imprint","INTERSECT",VERTEX,{"disambiguationData":[OD(1.0)],"derivedFrom":[sQuery(id+"F0.wireOp",EDGE,"E1"),subQ0]}),1.0]])],"derivedFrom":subQ0})])],"isStart":true});}
            var Q78;
            Q78=makeQuery(id+"F1.opExtrude","CAP_EDGE",EDGE,{"disambiguationData":[OSD([sQuery(id+"F0.wireOp",EDGE,"E12.1.3")])],"isStart":true});
            var Q79;
            Q79=makeQuery(id+"F1.opExtrude","CAP_EDGE",EDGE,{"disambiguationData":[OSD([sQuery(id+"F0.wireOp",EDGE,"E12.2.0")])],"isStart":true});
            var Q80;
            {var subQ0=sQuery(id+"F0.wireOp",EDGE,"E12.2.14");Q80=makeQuery(id+"F1.opExtrude","CAP_EDGE",EDGE,{"disambiguationData":[OSD([subQ0]),TDD([makeQuery(id+"F0.imprint","IMPRINT",EDGE,{"disambiguationData":[TD([[makeQuery(id+"F0.imprint","INTERSECT",VERTEX,{"disambiguationData":[OD(1.0)],"derivedFrom":[sQuery(id+"F0.wireOp",EDGE,"E1"),subQ0]}),-1.0]])],"derivedFrom":subQ0})])],"isStart":true});}
            var Q81;
            Q81=makeQuery(id+"F1.opExtrude","CAP_EDGE",EDGE,{"disambiguationData":[OSD([sQuery(id+"F0.wireOp",EDGE,"E15.3")])],"isStart":true});
            var Q82;
            {var subQ0=sQuery(id+"F0.wireOp",EDGE,"E7");var subQ1=sQuery(id+"F0.wireOp",EDGE,"E1");Q82=makeQuery(id+"F1.opExtrude","SWEPT_EDGE",EDGE,{"disambiguationData":[OSD([subQ1,subQ0]),TDD([makeQuery(id+"F0.imprint","INTERSECT",VERTEX,{"disambiguationData":[OD(1.0)],"derivedFrom":[subQ1,subQ0]})])]});}
            var Q83;
            Q83=makeQuery(id+"F1.opExtrude","SWEPT_EDGE",EDGE,{"disambiguationData":[OSD([sQuery(id+"F0.wireOp",EDGE,"E12.2.7"),sQuery(id+"F0.wireOp",EDGE,"E12.2.13")])]});
            var Q84;
            {var subQ0=sQuery(id+"F0.wireOp",EDGE,"E12.1.14");var subQ1=sQuery(id+"F0.wireOp",EDGE,"E1");Q84=makeQuery(id+"F1.opExtrude","SWEPT_EDGE",EDGE,{"disambiguationData":[OSD([subQ1,subQ0]),TDD([makeQuery(id+"F0.imprint","INTERSECT",VERTEX,{"disambiguationData":[OD(0.0)],"derivedFrom":[subQ1,subQ0]})])]});}
            var Q85;
            Q85=makeQuery(id+"F1.opExtrude","SWEPT_EDGE",EDGE,{"disambiguationData":[OSD([sQuery(id+"F0.wireOp",EDGE,"E12.2.14"),sQuery(id+"F0.wireOp",EDGE,"E14.2")])]});
            var Q86;
            {var subQ0=sQuery(id+"F0.wireOp",EDGE,"E7");Q86=makeQuery(id+"F1.opExtrude","CAP_EDGE",EDGE,{"disambiguationData":[OSD([subQ0]),TDD([makeQuery(id+"F0.imprint","IMPRINT",EDGE,{"disambiguationData":[TD([[makeQuery(id+"F0.imprint","INTERSECT",VERTEX,{"disambiguationData":[OD(0.0)],"derivedFrom":[sQuery(id+"F0.wireOp",EDGE,"E1"),subQ0]}),-1.0]])],"derivedFrom":subQ0})])],"isStart":true});}
            var Q87;
            Q87=makeQuery(id+"F1.opExtrude","CAP_EDGE",EDGE,{"disambiguationData":[OSD([sQuery(id+"F0.wireOp",EDGE,"E12.1.5")])],"isStart":true});
            var Q88;
            Q88=makeQuery(id+"F1.opExtrude","CAP_EDGE",EDGE,{"disambiguationData":[OSD([sQuery(id+"F0.wireOp",EDGE,"E13.2")])],"isStart":true});
            var Q89;
            Q89=makeQuery(id+"F1.opExtrude","CAP_EDGE",EDGE,{"disambiguationData":[OSD([sQuery(id+"F0.wireOp",EDGE,"E15.4")])],"isStart":true});
            var Q90;
            {var subQ0=sQuery(id+"F0.wireOp",EDGE,"E12.1.14");var subQ1=sQuery(id+"F0.wireOp",EDGE,"E1");Q90=makeQuery(id+"F1.opExtrude","SWEPT_EDGE",EDGE,{"disambiguationData":[OSD([subQ1,subQ0]),TDD([makeQuery(id+"F0.imprint","INTERSECT",VERTEX,{"disambiguationData":[OD(1.0)],"derivedFrom":[subQ1,subQ0]})])]});}
            var Q91;
            Q91=makeQuery(id+"F1.opExtrude","SWEPT_EDGE",EDGE,{"disambiguationData":[OSD([sQuery(id+"F0.wireOp",EDGE,"E12.2.14"),sQuery(id+"F0.wireOp",EDGE,"E14.4")])]});
            var Q92;
            {var subQ0=sQuery(id+"F0.wireOp",EDGE,"E12.2.14");var subQ1=sQuery(id+"F0.wireOp",EDGE,"E1");Q92=makeQuery(id+"F1.opExtrude","SWEPT_EDGE",EDGE,{"disambiguationData":[OSD([subQ1,subQ0]),TDD([makeQuery(id+"F0.imprint","INTERSECT",VERTEX,{"disambiguationData":[OD(1.0)],"derivedFrom":[subQ1,subQ0]})])]});}
            var Q93;
            Q93=makeQuery(id+"F1.opExtrude","CAP_EDGE",EDGE,{"disambiguationData":[OSD([sQuery(id+"F0.wireOp",EDGE,"E11.1")])],"isStart":true});
            var Q94;
            Q94=makeQuery(id+"F1.opExtrude","CAP_EDGE",EDGE,{"disambiguationData":[OSD([sQuery(id+"F0.wireOp",EDGE,"E12.2.5")])],"isStart":true});
            var Q95;
            Q95=makeQuery(id+"F1.opExtrude","CAP_EDGE",EDGE,{"disambiguationData":[OSD([sQuery(id+"F0.wireOp",EDGE,"E13.3")])],"isStart":true});
            var Q96;
            Q96=makeQuery(id+"F1.opExtrude","SWEPT_EDGE",EDGE,{"disambiguationData":[OSD([sQuery(id+"F0.wireOp",EDGE,"E6"),sQuery(id+"F0.wireOp",EDGE,"E11.1")])]});
            var Q97;
            Q97=makeQuery(id+"F1.opExtrude","SWEPT_EDGE",EDGE,{"disambiguationData":[OSD([sQuery(id+"F0.wireOp",EDGE,"E6"),sQuery(id+"F0.wireOp",EDGE,"E11.5")])]});
            var Q98;
            {var subQ0=sQuery(id+"F0.wireOp",EDGE,"E7");var subQ1=sQuery(id+"F0.wireOp",EDGE,"E1");Q98=makeQuery(id+"F1.opExtrude","CAP_EDGE",EDGE,{"disambiguationData":[OSD([subQ1]),TDD([makeQuery(id+"F0.imprint","IMPRINT",EDGE,{"disambiguationData":[TD([[makeQuery(id+"F0.imprint","INTERSECT",VERTEX,{"disambiguationData":[OD(0.0)],"derivedFrom":[subQ1,subQ0]}),-1.0]])],"derivedFrom":subQ1})])],"isStart":true});}
            var Q99;
            {var subQ0=sQuery(id+"F0.wireOp",EDGE,"E12.1.7");var subQ1=makeQuery(id+"F0.imprint","INTERSECT",VERTEX,{"disambiguationData":[OD(1.0)],"derivedFrom":[sQuery(id+"F0.wireOp",EDGE,"E1"),subQ0]});var subQ2=makeQuery(id+"F0.imprint","INTERSECT",VERTEX,{"derivedFrom":[subQ0,sQuery(id+"F0.wireOp",EDGE,"E15.5")]});Q99=makeQuery(id+"F1.opExtrude","CAP_EDGE",EDGE,{"disambiguationData":[OSD([subQ0]),TDD([makeQuery(id+"F0.imprint","IMPRINT",EDGE,{"disambiguationData":[TD([[subQ2,1.0]])],"derivedFrom":subQ0}),makeQuery(id+"F0.imprint","IMPRINT",EDGE,{"disambiguationData":[TD([[subQ1,1.0]])],"derivedFrom":subQ0}),makeQuery(id+"F0.imprint","IMPRINT",EDGE,{"disambiguationData":[TD([[subQ1,-1.0]])],"derivedFrom":subQ0})])],"isStart":true});}
            var Q100;
            {var subQ0=sQuery(id+"F0.wireOp",EDGE,"E12.2.7");var subQ1=makeQuery(id+"F0.imprint","INTERSECT",VERTEX,{"disambiguationData":[OD(1.0)],"derivedFrom":[sQuery(id+"F0.wireOp",EDGE,"E1"),subQ0]});var subQ2=makeQuery(id+"F0.imprint","INTERSECT",VERTEX,{"derivedFrom":[subQ0,sQuery(id+"F0.wireOp",EDGE,"E14.1")]});Q100=makeQuery(id+"F1.opExtrude","CAP_EDGE",EDGE,{"disambiguationData":[OSD([subQ0]),TDD([makeQuery(id+"F0.imprint","IMPRINT",EDGE,{"disambiguationData":[TD([[subQ2,-1.0]])],"derivedFrom":subQ0}),makeQuery(id+"F0.imprint","IMPRINT",EDGE,{"disambiguationData":[TD([[subQ1,1.0]])],"derivedFrom":subQ0}),makeQuery(id+"F0.imprint","IMPRINT",EDGE,{"disambiguationData":[TD([[subQ1,-1.0]])],"derivedFrom":subQ0})])],"isStart":true});}
            var Q101;
            Q101=makeQuery(id+"F1.opExtrude","SWEPT_EDGE",EDGE,{"disambiguationData":[OSD([sQuery(id+"F0.wireOp",EDGE,"E6"),sQuery(id+"F0.wireOp",EDGE,"E12.2.7")])]});
            var Q102;
            {var subQ0=sQuery(id+"F0.wireOp",EDGE,"E12.1.14");var subQ1=sQuery(id+"F0.wireOp",EDGE,"E1");Q102=makeQuery(id+"F1.opExtrude","CAP_EDGE",EDGE,{"disambiguationData":[OSD([subQ1]),TDD([makeQuery(id+"F0.imprint","IMPRINT",EDGE,{"disambiguationData":[TD([[makeQuery(id+"F0.imprint","INTERSECT",VERTEX,{"disambiguationData":[OD(0.0)],"derivedFrom":[subQ1,subQ0]}),-1.0]])],"derivedFrom":subQ1})])],"isStart":true});}
            var Q103;
            {var subQ0=sQuery(id+"F0.wireOp",EDGE,"E12.2.7");var subQ1=makeQuery(id+"F0.imprint","INTERSECT",VERTEX,{"disambiguationData":[OD(0.0)],"derivedFrom":[sQuery(id+"F0.wireOp",EDGE,"E1"),subQ0]});var subQ2=makeQuery(id+"F0.imprint","INTERSECT",VERTEX,{"derivedFrom":[subQ0,sQuery(id+"F0.wireOp",EDGE,"E14.5")]});Q103=makeQuery(id+"F1.opExtrude","CAP_EDGE",EDGE,{"disambiguationData":[OSD([subQ0]),TDD([makeQuery(id+"F0.imprint","IMPRINT",EDGE,{"disambiguationData":[TD([[subQ2,1.0]])],"derivedFrom":subQ0}),makeQuery(id+"F0.imprint","IMPRINT",EDGE,{"disambiguationData":[TD([[subQ1,1.0]])],"derivedFrom":subQ0}),makeQuery(id+"F0.imprint","IMPRINT",EDGE,{"disambiguationData":[TD([[subQ1,-1.0]])],"derivedFrom":subQ0})])],"isStart":true});}
            var Q104;
            Q104=makeQuery(id+"F1.opExtrude","SWEPT_EDGE",EDGE,{"disambiguationData":[OSD([sQuery(id+"F0.wireOp",EDGE,"E7"),sQuery(id+"F0.wireOp",EDGE,"E13.2")])]});
            var Q105;
            Q105=makeQuery(id+"F1.opExtrude","SWEPT_EDGE",EDGE,{"disambiguationData":[OSD([sQuery(id+"F0.wireOp",EDGE,"E11.1"),sQuery(id+"F0.wireOp",EDGE,"E11.2")])]});
            var Q106;
            Q106=makeQuery(id+"F1.opExtrude","SWEPT_EDGE",EDGE,{"disambiguationData":[OSD([sQuery(id+"F0.wireOp",EDGE,"E11.2"),sQuery(id+"F0.wireOp",EDGE,"E11.3")])]});
            var Q107;
            Q107=makeQuery(id+"F1.opExtrude","SWEPT_EDGE",EDGE,{"disambiguationData":[OSD([sQuery(id+"F0.wireOp",EDGE,"E12.1.0"),sQuery(id+"F0.wireOp",EDGE,"E12.1.11")])]});
            var Q108;
            Q108=makeQuery(id+"F1.opExtrude","SWEPT_EDGE",EDGE,{"disambiguationData":[OSD([sQuery(id+"F0.wireOp",EDGE,"E12.1.0"),sQuery(id+"F0.wireOp",EDGE,"E12.1.5")])]});
            var Q109;
            Q109=makeQuery(id+"F1.opExtrude","SWEPT_EDGE",EDGE,{"disambiguationData":[OSD([sQuery(id+"F0.wireOp",EDGE,"E12.1.3"),sQuery(id+"F0.wireOp",EDGE,"E12.1.5")])]});
            var Q110;
            Q110=makeQuery(id+"F1.opExtrude","SWEPT_EDGE",EDGE,{"disambiguationData":[OSD([sQuery(id+"F0.wireOp",EDGE,"E12.2.3"),sQuery(id+"F0.wireOp",EDGE,"E12.2.13")])]});
            var Q111;
            Q111=makeQuery(id+"F1.opExtrude","SWEPT_EDGE",EDGE,{"disambiguationData":[OSD([sQuery(id+"F0.wireOp",EDGE,"E7"),sQuery(id+"F0.wireOp",EDGE,"E13.4")])]});
            var Q112;
            {var subQ0=sQuery(id+"F0.wireOp",EDGE,"E12.2.14");var subQ1=sQuery(id+"F0.wireOp",EDGE,"E1");Q112=makeQuery(id+"F1.opExtrude","SWEPT_EDGE",EDGE,{"disambiguationData":[OSD([subQ1,subQ0]),TDD([makeQuery(id+"F0.imprint","INTERSECT",VERTEX,{"disambiguationData":[OD(0.0)],"derivedFrom":[subQ1,subQ0]})])]});}
            var Q113;
            Q113=makeQuery(id+"F1.opExtrude","CAP_EDGE",EDGE,{"disambiguationData":[OSD([sQuery(id+"F0.wireOp",EDGE,"E11.2")])],"isStart":true});
            var Q114;
            Q114=makeQuery(id+"F1.opExtrude","CAP_EDGE",EDGE,{"disambiguationData":[OSD([sQuery(id+"F0.wireOp",EDGE,"E13.4")])],"isStart":true});
            var Q115;
            Q115=makeQuery(id+"F1.opExtrude","SWEPT_EDGE",EDGE,{"disambiguationData":[OSD([sQuery(id+"F0.wireOp",EDGE,"E6"),sQuery(id+"F0.wireOp",EDGE,"E12.1.7")])]});
            var Q116;
            Q116=makeQuery(id+"F1.opExtrude","CAP_EDGE",EDGE,{"disambiguationData":[OSD([sQuery(id+"F0.wireOp",EDGE,"E14.2")])],"isStart":true});
            chamfer(context, id + "F2", {"entities" : qUnion([Q0, Q1, Q2, Q3, Q4, Q5, Q6, Q7, Q8, Q9, Q10, Q11, Q12, Q13, Q14, Q15, Q16, Q17, Q18, Q19, Q20, Q21, Q22, Q23, Q24, Q25, Q26, Q27, Q28, Q29, Q30, Q31, Q32, Q33, Q34, Q35, Q36, Q37, Q38, Q39, Q40, Q41, Q42, Q43, Q44, Q45, Q46, Q47, Q48, Q49, Q50, Q51, Q52, Q53, Q54, Q55, Q56, Q57, Q58, Q59, Q60, Q61, Q62, Q63, Q64, Q65, Q66, Q67, Q68, Q69, Q70, Q71, Q72, Q73, Q74, Q75, Q76, Q77, Q78, Q79, Q80, Q81, Q82, Q83, Q84, Q85, Q86, Q87, Q88, Q89, Q90, Q91, Q92, Q93, Q94, Q95, Q96, Q97, Q98, Q99, Q100, Q101, Q102, Q103, Q104, Q105, Q106, Q107, Q108, Q109, Q110, Q111, Q112, Q113, Q114, Q115, Q116]), "width" : 0.64 * mm, "tangentPropagation" : true});
        }
    });
